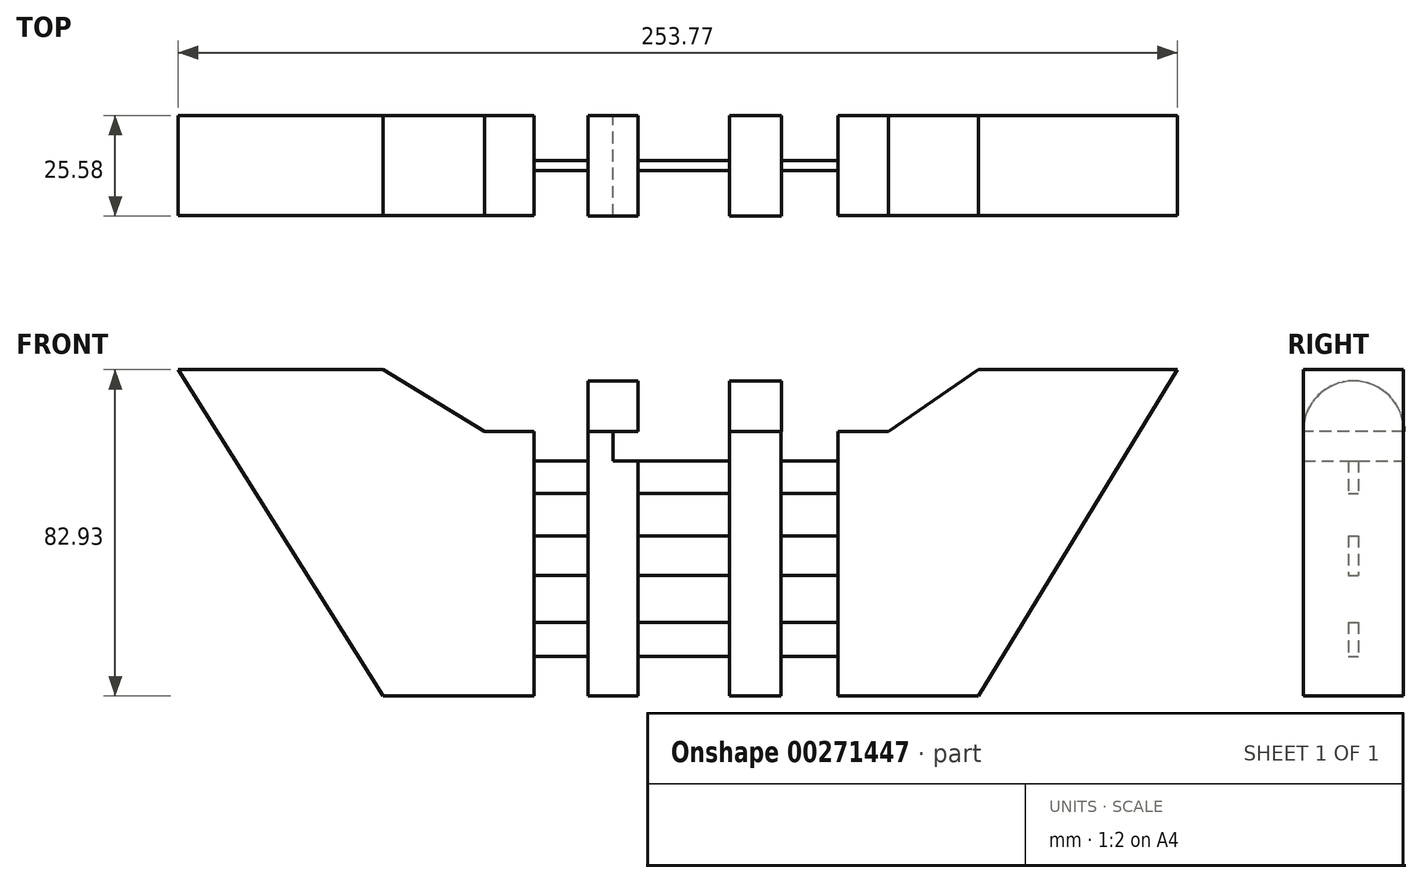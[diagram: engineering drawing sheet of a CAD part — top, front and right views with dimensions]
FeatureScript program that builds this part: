
annotation { "Feature Type Name" : "Feature", "Feature Type Description" : "" }
export const myFeature = defineFeature(function(context is Context, id is Id, definition is map)
    precondition{}
    {
        {
            var Q0;
            Q0=qCreatedBy(makeId("Front.planeOp"),FACE);
            var sketch = newSketch(context, id + "F0", { "sketchPlane" : qUnion([Q0])});
            skLineSegment(sketch, "E0", {"start": v(-135.53, 39.83) * mm, "end": v(-135.53, -55.88) * mm});
            skLineSegment(sketch, "E1", {"start": v(-135.53, -55.88) * mm, "end": v(134.04, -55.88) * mm});
            skLineSegment(sketch, "E2", {"start": v(134.04, -55.88) * mm, "end": v(134.04, 39.83) * mm});
            skLineSegment(sketch, "E3", {"start": v(-135.53, 39.83) * mm, "end": v(-75.5, -55.88) * mm});
            skLineSegment(sketch, "E4", {"start": v(134.04, 39.83) * mm, "end": v(75.79, -55.88) * mm});
            skLineSegment(sketch, "E5", {"start": v(-135.53, 27.05) * mm, "end": v(134.04, 27.05) * mm});
            skLineSegment(sketch, "E6", {"start": v(-75.5, 27.05) * mm, "end": v(-49.76, 11.38) * mm});
            skLineSegment(sketch, "E7", {"start": v(-49.76, 11.38) * mm, "end": v(-37.15, 11.38) * mm});
            skLineSegment(sketch, "E8", {"start": v(-37.15, 11.38) * mm, "end": v(-37.15, -55.88) * mm});
            skLineSegment(sketch, "E9", {"start": v(75.79, 27.05) * mm, "end": v(52.9, 11.38) * mm});
            skPoint(sketch, "E9.endSnap0", {"position": v(-43.46, 11.38) * mm});
            skLineSegment(sketch, "E10", {"start": v(52.9, 11.38) * mm, "end": v(40.12, 11.38) * mm});
            skLineSegment(sketch, "E11", {"start": v(40.12, 11.38) * mm, "end": v(40.12, -55.88) * mm});
            skLineSegment(sketch, "E12", {"start": v(-37.15, 11.38) * mm, "end": v(40.12, 11.38) * mm});
            skLineSegment(sketch, "E13", {"start": v(-23.48, -55.88) * mm, "end": v(-23.48, 11.38) * mm});
            skLineSegment(sketch, "E14", {"start": v(-23.48, 11.38) * mm, "end": v(-10.7, 11.38) * mm});
            skLineSegment(sketch, "E15", {"start": v(-10.7, 11.38) * mm, "end": v(-10.7, -55.88) * mm});
            skLineSegment(sketch, "E16", {"start": v(25.56, -55.88) * mm, "end": v(25.56, 11.38) * mm});
            skLineSegment(sketch, "E17", {"start": v(25.56, 11.38) * mm, "end": v(12.48, 11.38) * mm});
            skLineSegment(sketch, "E18", {"start": v(12.48, 11.38) * mm, "end": v(12.48, -55.88) * mm});
            skLineSegment(sketch, "E19", {"start": v(-23.48, 11.38) * mm, "end": v(-23.48, 16.64) * mm});
            skLineSegment(sketch, "E20", {"start": v(-23.48, 16.64) * mm, "end": v(-10.7, 16.64) * mm});
            skLineSegment(sketch, "E21", {"start": v(-10.7, 16.64) * mm, "end": v(-10.7, 11.38) * mm});
            skLineSegment(sketch, "E22", {"start": v(12.48, 11.38) * mm, "end": v(12.48, 16.64) * mm});
            skLineSegment(sketch, "E23", {"start": v(12.48, 16.64) * mm, "end": v(25.56, 16.64) * mm});
            skLineSegment(sketch, "E24", {"start": v(25.56, 16.64) * mm, "end": v(25.56, 11.38) * mm});
            skLineSegment(sketch, "E25", {"start": v(-37.15, 3.86) * mm, "end": v(40.12, 3.86) * mm});
            skLineSegment(sketch, "E26", {"start": v(-37.15, -4.46) * mm, "end": v(40.12, -4.46) * mm});
            skLineSegment(sketch, "E27", {"start": v(-37.15, -15.16) * mm, "end": v(40.12, -15.16) * mm});
            skLineSegment(sketch, "E28", {"start": v(-37.15, -25.26) * mm, "end": v(40.12, -25.26) * mm});
            skLineSegment(sketch, "E29", {"start": v(-37.15, -37.15) * mm, "end": v(40.12, -37.15) * mm});
            skLineSegment(sketch, "E30", {"start": v(-37.15, -45.77) * mm, "end": v(40.12, -45.77) * mm});
            skLineSegment(sketch, "E31", {"start": v(-17.09, -55.88) * mm, "end": v(-17.09, 35.3) * mm});
            skPoint(sketch, "E31.startSnap0", {"position": v(-17.09, 11.38) * mm});
            skLineSegment(sketch, "E32", {"start": v(19.02, -55.88) * mm, "end": v(19.02, 35.3) * mm});
            skPoint(sketch, "E32.startSnap0", {"position": v(19.02, 11.38) * mm});
            skLineSegment(sketch, "E33.bottom", {"start": v(-23.48, 11.38) * mm, "end": v(-10.72, 11.38) * mm});
            skLineSegment(sketch, "E33.top", {"start": v(-23.48, 24.18) * mm, "end": v(-10.72, 24.18) * mm});
            skLineSegment(sketch, "E33.left", {"start": v(-23.48, 11.38) * mm, "end": v(-23.48, 24.18) * mm});
            skLineSegment(sketch, "E33.right", {"start": v(-10.72, 11.38) * mm, "end": v(-10.72, 24.18) * mm});
            skLineSegment(sketch, "E34.bottom", {"start": v(12.48, 11.38) * mm, "end": v(25.74, 11.38) * mm});
            skLineSegment(sketch, "E34.top", {"start": v(12.48, 24.18) * mm, "end": v(25.74, 24.18) * mm});
            skLineSegment(sketch, "E34.left", {"start": v(12.48, 11.38) * mm, "end": v(12.48, 24.18) * mm});
            skLineSegment(sketch, "E34.right", {"start": v(25.74, 11.38) * mm, "end": v(25.74, 24.18) * mm});
            skSolve(sketch);
        }
        {
            var Q0;
            {var subQ4=sQuery(id+"F0.wireOp",EDGE,"E6");Q0=makeQuery(id+"F0.imprint","IMPRINT",FACE,{"disambiguationData":[TD([[makeQuery(id+"F0.imprint","IMPRINT",EDGE,{"derivedFrom":subQ4}),-1.0]])]});}
            var Q1;
            {var subQ5=sQuery(id+"F0.wireOp",EDGE,"E9");Q1=makeQuery(id+"F0.imprint","IMPRINT",FACE,{"disambiguationData":[TD([[makeQuery(id+"F0.imprint","IMPRINT",EDGE,{"derivedFrom":subQ5}),1.0]])]});}
            var Q2;
            {var subQ0=sQuery(id+"F0.wireOp",EDGE,"E27");var subQ1=sQuery(id+"F0.wireOp",EDGE,"E13");var subQ2=makeQuery(id+"F0.imprint","INTERSECT",VERTEX,{"derivedFrom":[subQ1,subQ0]});Q2=makeQuery(id+"F0.imprint","IMPRINT",FACE,{"disambiguationData":[TD([[makeQuery(id+"F0.imprint","IMPRINT",EDGE,{"disambiguationData":[TD([[subQ2,-1.0]])],"derivedFrom":subQ1}),-1.0]])]});}
            var Q3;
            {var subQ0=sQuery(id+"F0.wireOp",EDGE,"E26");var subQ1=sQuery(id+"F0.wireOp",EDGE,"E13");var subQ2=makeQuery(id+"F0.imprint","INTERSECT",VERTEX,{"derivedFrom":[subQ1,subQ0]});Q3=makeQuery(id+"F0.imprint","IMPRINT",FACE,{"disambiguationData":[TD([[makeQuery(id+"F0.imprint","IMPRINT",EDGE,{"disambiguationData":[TD([[subQ2,-1.0]])],"derivedFrom":subQ1}),-1.0]])]});}
            var Q4;
            {var subQ0=sQuery(id+"F0.wireOp",EDGE,"E28");var subQ1=sQuery(id+"F0.wireOp",EDGE,"E13");var subQ2=makeQuery(id+"F0.imprint","INTERSECT",VERTEX,{"derivedFrom":[subQ1,subQ0]});Q4=makeQuery(id+"F0.imprint","IMPRINT",FACE,{"disambiguationData":[TD([[makeQuery(id+"F0.imprint","IMPRINT",EDGE,{"disambiguationData":[TD([[subQ2,-1.0]])],"derivedFrom":subQ1}),-1.0]])]});}
            var Q5;
            {var subQ0=sQuery(id+"F0.wireOp",EDGE,"E29");var subQ1=sQuery(id+"F0.wireOp",EDGE,"E13");var subQ2=makeQuery(id+"F0.imprint","INTERSECT",VERTEX,{"derivedFrom":[subQ1,subQ0]});Q5=makeQuery(id+"F0.imprint","IMPRINT",FACE,{"disambiguationData":[TD([[makeQuery(id+"F0.imprint","IMPRINT",EDGE,{"disambiguationData":[TD([[subQ2,-1.0]])],"derivedFrom":subQ1}),-1.0]])]});}
            var Q6;
            {var subQ0=sQuery(id+"F0.wireOp",EDGE,"E30");var subQ1=sQuery(id+"F0.wireOp",EDGE,"E13");var subQ2=makeQuery(id+"F0.imprint","INTERSECT",VERTEX,{"derivedFrom":[subQ1,subQ0]});Q6=makeQuery(id+"F0.imprint","IMPRINT",FACE,{"disambiguationData":[TD([[makeQuery(id+"F0.imprint","IMPRINT",EDGE,{"disambiguationData":[TD([[subQ2,-1.0]])],"derivedFrom":subQ1}),-1.0]])]});}
            var Q7;
            {var subQ0=sQuery(id+"F0.wireOp",EDGE,"E13");var subQ1=sQuery(id+"F0.wireOp",EDGE,"E1");var subQ2=makeQuery(id+"F0.imprint","INTERSECT",VERTEX,{"derivedFrom":[subQ1,subQ0]});Q7=makeQuery(id+"F0.imprint","IMPRINT",FACE,{"disambiguationData":[TD([[makeQuery(id+"F0.imprint","IMPRINT",EDGE,{"disambiguationData":[TD([[subQ2,-1.0]])],"derivedFrom":subQ1}),1.0]])]});}
            var Q8;
            {var subQ0=sQuery(id+"F0.wireOp",EDGE,"E17");Q8=makeQuery(id+"F0.imprint","IMPRINT",FACE,{"disambiguationData":[TD([[makeQuery(id+"F0.imprint","IMPRINT",EDGE,{"derivedFrom":subQ0}),1.0]])]});}
            var Q9;
            {var subQ0=sQuery(id+"F0.wireOp",EDGE,"E26");var subQ1=sQuery(id+"F0.wireOp",EDGE,"E16");var subQ2=makeQuery(id+"F0.imprint","INTERSECT",VERTEX,{"derivedFrom":[subQ1,subQ0]});Q9=makeQuery(id+"F0.imprint","IMPRINT",FACE,{"disambiguationData":[TD([[makeQuery(id+"F0.imprint","IMPRINT",EDGE,{"disambiguationData":[TD([[subQ2,-1.0]])],"derivedFrom":subQ1}),1.0]])]});}
            var Q10;
            {var subQ0=sQuery(id+"F0.wireOp",EDGE,"E27");var subQ1=sQuery(id+"F0.wireOp",EDGE,"E16");var subQ2=makeQuery(id+"F0.imprint","INTERSECT",VERTEX,{"derivedFrom":[subQ1,subQ0]});Q10=makeQuery(id+"F0.imprint","IMPRINT",FACE,{"disambiguationData":[TD([[makeQuery(id+"F0.imprint","IMPRINT",EDGE,{"disambiguationData":[TD([[subQ2,-1.0]])],"derivedFrom":subQ1}),1.0]])]});}
            var Q11;
            {var subQ0=sQuery(id+"F0.wireOp",EDGE,"E28");var subQ1=sQuery(id+"F0.wireOp",EDGE,"E16");var subQ2=makeQuery(id+"F0.imprint","INTERSECT",VERTEX,{"derivedFrom":[subQ1,subQ0]});Q11=makeQuery(id+"F0.imprint","IMPRINT",FACE,{"disambiguationData":[TD([[makeQuery(id+"F0.imprint","IMPRINT",EDGE,{"disambiguationData":[TD([[subQ2,-1.0]])],"derivedFrom":subQ1}),1.0]])]});}
            var Q12;
            {var subQ0=sQuery(id+"F0.wireOp",EDGE,"E29");var subQ1=sQuery(id+"F0.wireOp",EDGE,"E16");var subQ2=makeQuery(id+"F0.imprint","INTERSECT",VERTEX,{"derivedFrom":[subQ1,subQ0]});Q12=makeQuery(id+"F0.imprint","IMPRINT",FACE,{"disambiguationData":[TD([[makeQuery(id+"F0.imprint","IMPRINT",EDGE,{"disambiguationData":[TD([[subQ2,-1.0]])],"derivedFrom":subQ1}),1.0]])]});}
            var Q13;
            {var subQ0=sQuery(id+"F0.wireOp",EDGE,"E30");var subQ1=sQuery(id+"F0.wireOp",EDGE,"E16");var subQ2=makeQuery(id+"F0.imprint","INTERSECT",VERTEX,{"derivedFrom":[subQ1,subQ0]});Q13=makeQuery(id+"F0.imprint","IMPRINT",FACE,{"disambiguationData":[TD([[makeQuery(id+"F0.imprint","IMPRINT",EDGE,{"disambiguationData":[TD([[subQ2,-1.0]])],"derivedFrom":subQ1}),1.0]])]});}
            var Q14;
            {var subQ0=sQuery(id+"F0.wireOp",EDGE,"E16");var subQ1=sQuery(id+"F0.wireOp",EDGE,"E1");var subQ2=makeQuery(id+"F0.imprint","INTERSECT",VERTEX,{"derivedFrom":[subQ1,subQ0]});Q14=makeQuery(id+"F0.imprint","IMPRINT",FACE,{"disambiguationData":[TD([[makeQuery(id+"F0.imprint","IMPRINT",EDGE,{"disambiguationData":[TD([[subQ2,1.0]])],"derivedFrom":subQ1}),1.0]])]});}
            var Q15;
            {var subQ0=sQuery(id+"F0.wireOp",EDGE,"E14");Q15=makeQuery(id+"F0.imprint","IMPRINT",FACE,{"disambiguationData":[TD([[makeQuery(id+"F0.imprint","IMPRINT",EDGE,{"derivedFrom":subQ0}),-1.0]])]});}
            var Q16;
            {var subQ0=sQuery(id+"F0.wireOp",EDGE,"E25");var subQ1=sQuery(id+"F0.wireOp",EDGE,"E15");var subQ2=makeQuery(id+"F0.imprint","INTERSECT",VERTEX,{"derivedFrom":[subQ1,subQ0]});Q16=makeQuery(id+"F0.imprint","IMPRINT",FACE,{"disambiguationData":[TD([[makeQuery(id+"F0.imprint","IMPRINT",EDGE,{"disambiguationData":[TD([[subQ2,-1.0]])],"derivedFrom":subQ1}),-1.0]])]});}
            var Q17;
            {var subQ0=sQuery(id+"F0.wireOp",EDGE,"E26");var subQ1=sQuery(id+"F0.wireOp",EDGE,"E15");var subQ2=makeQuery(id+"F0.imprint","INTERSECT",VERTEX,{"derivedFrom":[subQ1,subQ0]});Q17=makeQuery(id+"F0.imprint","IMPRINT",FACE,{"disambiguationData":[TD([[makeQuery(id+"F0.imprint","IMPRINT",EDGE,{"disambiguationData":[TD([[subQ2,-1.0]])],"derivedFrom":subQ1}),-1.0]])]});}
            var Q18;
            {var subQ0=sQuery(id+"F0.wireOp",EDGE,"E27");var subQ1=sQuery(id+"F0.wireOp",EDGE,"E15");var subQ2=makeQuery(id+"F0.imprint","INTERSECT",VERTEX,{"derivedFrom":[subQ1,subQ0]});Q18=makeQuery(id+"F0.imprint","IMPRINT",FACE,{"disambiguationData":[TD([[makeQuery(id+"F0.imprint","IMPRINT",EDGE,{"disambiguationData":[TD([[subQ2,-1.0]])],"derivedFrom":subQ1}),-1.0]])]});}
            var Q19;
            {var subQ0=sQuery(id+"F0.wireOp",EDGE,"E28");var subQ1=sQuery(id+"F0.wireOp",EDGE,"E15");var subQ2=makeQuery(id+"F0.imprint","INTERSECT",VERTEX,{"derivedFrom":[subQ1,subQ0]});Q19=makeQuery(id+"F0.imprint","IMPRINT",FACE,{"disambiguationData":[TD([[makeQuery(id+"F0.imprint","IMPRINT",EDGE,{"disambiguationData":[TD([[subQ2,-1.0]])],"derivedFrom":subQ1}),-1.0]])]});}
            var Q20;
            {var subQ0=sQuery(id+"F0.wireOp",EDGE,"E29");var subQ1=sQuery(id+"F0.wireOp",EDGE,"E15");var subQ2=makeQuery(id+"F0.imprint","INTERSECT",VERTEX,{"derivedFrom":[subQ1,subQ0]});Q20=makeQuery(id+"F0.imprint","IMPRINT",FACE,{"disambiguationData":[TD([[makeQuery(id+"F0.imprint","IMPRINT",EDGE,{"disambiguationData":[TD([[subQ2,-1.0]])],"derivedFrom":subQ1}),-1.0]])]});}
            var Q21;
            {var subQ0=sQuery(id+"F0.wireOp",EDGE,"E15");var subQ1=sQuery(id+"F0.wireOp",EDGE,"E1");var subQ2=makeQuery(id+"F0.imprint","INTERSECT",VERTEX,{"derivedFrom":[subQ1,subQ0]});Q21=makeQuery(id+"F0.imprint","IMPRINT",FACE,{"disambiguationData":[TD([[makeQuery(id+"F0.imprint","IMPRINT",EDGE,{"disambiguationData":[TD([[subQ2,1.0]])],"derivedFrom":subQ1}),1.0]])]});}
            var Q22;
            {var subQ0=sQuery(id+"F0.wireOp",EDGE,"E25");var subQ1=sQuery(id+"F0.wireOp",EDGE,"E18");var subQ2=makeQuery(id+"F0.imprint","INTERSECT",VERTEX,{"derivedFrom":[subQ1,subQ0]});Q22=makeQuery(id+"F0.imprint","IMPRINT",FACE,{"disambiguationData":[TD([[makeQuery(id+"F0.imprint","IMPRINT",EDGE,{"disambiguationData":[TD([[subQ2,-1.0]])],"derivedFrom":subQ1}),1.0]])]});}
            var Q23;
            {var subQ0=sQuery(id+"F0.wireOp",EDGE,"E26");var subQ1=sQuery(id+"F0.wireOp",EDGE,"E18");var subQ2=makeQuery(id+"F0.imprint","INTERSECT",VERTEX,{"derivedFrom":[subQ1,subQ0]});Q23=makeQuery(id+"F0.imprint","IMPRINT",FACE,{"disambiguationData":[TD([[makeQuery(id+"F0.imprint","IMPRINT",EDGE,{"disambiguationData":[TD([[subQ2,-1.0]])],"derivedFrom":subQ1}),1.0]])]});}
            var Q24;
            {var subQ0=sQuery(id+"F0.wireOp",EDGE,"E27");var subQ1=sQuery(id+"F0.wireOp",EDGE,"E18");var subQ2=makeQuery(id+"F0.imprint","INTERSECT",VERTEX,{"derivedFrom":[subQ1,subQ0]});Q24=makeQuery(id+"F0.imprint","IMPRINT",FACE,{"disambiguationData":[TD([[makeQuery(id+"F0.imprint","IMPRINT",EDGE,{"disambiguationData":[TD([[subQ2,-1.0]])],"derivedFrom":subQ1}),1.0]])]});}
            var Q25;
            {var subQ0=sQuery(id+"F0.wireOp",EDGE,"E28");var subQ1=sQuery(id+"F0.wireOp",EDGE,"E18");var subQ2=makeQuery(id+"F0.imprint","INTERSECT",VERTEX,{"derivedFrom":[subQ1,subQ0]});Q25=makeQuery(id+"F0.imprint","IMPRINT",FACE,{"disambiguationData":[TD([[makeQuery(id+"F0.imprint","IMPRINT",EDGE,{"disambiguationData":[TD([[subQ2,-1.0]])],"derivedFrom":subQ1}),1.0]])]});}
            var Q26;
            {var subQ0=sQuery(id+"F0.wireOp",EDGE,"E29");var subQ1=sQuery(id+"F0.wireOp",EDGE,"E18");var subQ2=makeQuery(id+"F0.imprint","INTERSECT",VERTEX,{"derivedFrom":[subQ1,subQ0]});Q26=makeQuery(id+"F0.imprint","IMPRINT",FACE,{"disambiguationData":[TD([[makeQuery(id+"F0.imprint","IMPRINT",EDGE,{"disambiguationData":[TD([[subQ2,-1.0]])],"derivedFrom":subQ1}),1.0]])]});}
            var Q27;
            {var subQ0=sQuery(id+"F0.wireOp",EDGE,"E18");var subQ1=sQuery(id+"F0.wireOp",EDGE,"E1");var subQ2=makeQuery(id+"F0.imprint","INTERSECT",VERTEX,{"derivedFrom":[subQ1,subQ0]});Q27=makeQuery(id+"F0.imprint","IMPRINT",FACE,{"disambiguationData":[TD([[makeQuery(id+"F0.imprint","IMPRINT",EDGE,{"disambiguationData":[TD([[subQ2,-1.0]])],"derivedFrom":subQ1}),1.0]])]});}
            var Q28;
            {var subQ1=sQuery(id+"F0.wireOp",EDGE,"E13");var subQ3=sQuery(id+"F0.wireOp",EDGE,"E25");var subQ4=makeQuery(id+"F0.imprint","INTERSECT",VERTEX,{"derivedFrom":[subQ1,subQ3]});Q28=makeQuery(id+"F0.imprint","IMPRINT",FACE,{"disambiguationData":[TD([[makeQuery(id+"F0.imprint","IMPRINT",EDGE,{"disambiguationData":[TD([[subQ4,-1.0]])],"derivedFrom":subQ3}),1.0]])]});}
            var Q29;
            {var subQ1=sQuery(id+"F0.wireOp",EDGE,"E18");var subQ3=sQuery(id+"F0.wireOp",EDGE,"E25");var subQ4=makeQuery(id+"F0.imprint","INTERSECT",VERTEX,{"derivedFrom":[subQ1,subQ3]});Q29=makeQuery(id+"F0.imprint","IMPRINT",FACE,{"disambiguationData":[TD([[makeQuery(id+"F0.imprint","IMPRINT",EDGE,{"disambiguationData":[TD([[subQ4,-1.0]])],"derivedFrom":subQ3}),1.0]])]});}
            var Q30;
            {var subQ1=sQuery(id+"F0.wireOp",EDGE,"E16");var subQ3=sQuery(id+"F0.wireOp",EDGE,"E25");var subQ4=makeQuery(id+"F0.imprint","INTERSECT",VERTEX,{"derivedFrom":[subQ1,subQ3]});Q30=makeQuery(id+"F0.imprint","IMPRINT",FACE,{"disambiguationData":[TD([[makeQuery(id+"F0.imprint","IMPRINT",EDGE,{"disambiguationData":[TD([[subQ4,1.0]])],"derivedFrom":subQ3}),1.0]])]});}
            extrude(context, id + "F1", {"entities" : qUnion([Q0, Q1, Q2, Q3, Q4, Q5, Q6, Q7, Q8, Q9, Q10, Q11, Q12, Q13, Q14, Q15, Q16, Q17, Q18, Q19, Q20, Q21, Q22, Q23, Q24, Q25, Q26, Q27, Q28, Q29, Q30]), "endBound" : BoundingType.SYMMETRIC, "depth" : 25.4 * mm});
        }
        {
            var Q0;
            {var subQ0=sQuery(id+"F0.wireOp",EDGE,"E25");var subQ1=sQuery(id+"F0.wireOp",EDGE,"E8");var subQ2=makeQuery(id+"F0.imprint","INTERSECT",VERTEX,{"derivedFrom":[subQ1,subQ0]});Q0=makeQuery(id+"F0.imprint","IMPRINT",FACE,{"disambiguationData":[TD([[makeQuery(id+"F0.imprint","IMPRINT",EDGE,{"disambiguationData":[TD([[subQ2,-1.0]])],"derivedFrom":subQ1}),1.0]])]});}
            var Q1;
            {var subQ0=sQuery(id+"F0.wireOp",EDGE,"E25");var subQ1=sQuery(id+"F0.wireOp",EDGE,"E15");var subQ2=makeQuery(id+"F0.imprint","INTERSECT",VERTEX,{"derivedFrom":[subQ1,subQ0]});Q1=makeQuery(id+"F0.imprint","IMPRINT",FACE,{"disambiguationData":[TD([[makeQuery(id+"F0.imprint","IMPRINT",EDGE,{"disambiguationData":[TD([[subQ2,-1.0]])],"derivedFrom":subQ1}),1.0]])]});}
            var Q2;
            {var subQ0=sQuery(id+"F0.wireOp",EDGE,"E25");var subQ1=sQuery(id+"F0.wireOp",EDGE,"E11");var subQ2=makeQuery(id+"F0.imprint","INTERSECT",VERTEX,{"derivedFrom":[subQ1,subQ0]});Q2=makeQuery(id+"F0.imprint","IMPRINT",FACE,{"disambiguationData":[TD([[makeQuery(id+"F0.imprint","IMPRINT",EDGE,{"disambiguationData":[TD([[subQ2,-1.0]])],"derivedFrom":subQ1}),-1.0]])]});}
            var Q3;
            {var subQ0=sQuery(id+"F0.wireOp",EDGE,"E27");var subQ1=sQuery(id+"F0.wireOp",EDGE,"E8");var subQ2=makeQuery(id+"F0.imprint","INTERSECT",VERTEX,{"derivedFrom":[subQ1,subQ0]});Q3=makeQuery(id+"F0.imprint","IMPRINT",FACE,{"disambiguationData":[TD([[makeQuery(id+"F0.imprint","IMPRINT",EDGE,{"disambiguationData":[TD([[subQ2,-1.0]])],"derivedFrom":subQ1}),1.0]])]});}
            var Q4;
            {var subQ0=sQuery(id+"F0.wireOp",EDGE,"E29");var subQ1=sQuery(id+"F0.wireOp",EDGE,"E8");var subQ2=makeQuery(id+"F0.imprint","INTERSECT",VERTEX,{"derivedFrom":[subQ1,subQ0]});Q4=makeQuery(id+"F0.imprint","IMPRINT",FACE,{"disambiguationData":[TD([[makeQuery(id+"F0.imprint","IMPRINT",EDGE,{"disambiguationData":[TD([[subQ2,-1.0]])],"derivedFrom":subQ1}),1.0]])]});}
            var Q5;
            {var subQ0=sQuery(id+"F0.wireOp",EDGE,"E27");var subQ1=sQuery(id+"F0.wireOp",EDGE,"E15");var subQ2=makeQuery(id+"F0.imprint","INTERSECT",VERTEX,{"derivedFrom":[subQ1,subQ0]});Q5=makeQuery(id+"F0.imprint","IMPRINT",FACE,{"disambiguationData":[TD([[makeQuery(id+"F0.imprint","IMPRINT",EDGE,{"disambiguationData":[TD([[subQ2,-1.0]])],"derivedFrom":subQ1}),1.0]])]});}
            var Q6;
            {var subQ0=sQuery(id+"F0.wireOp",EDGE,"E29");var subQ1=sQuery(id+"F0.wireOp",EDGE,"E15");var subQ2=makeQuery(id+"F0.imprint","INTERSECT",VERTEX,{"derivedFrom":[subQ1,subQ0]});Q6=makeQuery(id+"F0.imprint","IMPRINT",FACE,{"disambiguationData":[TD([[makeQuery(id+"F0.imprint","IMPRINT",EDGE,{"disambiguationData":[TD([[subQ2,-1.0]])],"derivedFrom":subQ1}),1.0]])]});}
            var Q7;
            {var subQ0=sQuery(id+"F0.wireOp",EDGE,"E27");var subQ1=sQuery(id+"F0.wireOp",EDGE,"E11");var subQ2=makeQuery(id+"F0.imprint","INTERSECT",VERTEX,{"derivedFrom":[subQ1,subQ0]});Q7=makeQuery(id+"F0.imprint","IMPRINT",FACE,{"disambiguationData":[TD([[makeQuery(id+"F0.imprint","IMPRINT",EDGE,{"disambiguationData":[TD([[subQ2,-1.0]])],"derivedFrom":subQ1}),-1.0]])]});}
            var Q8;
            {var subQ0=sQuery(id+"F0.wireOp",EDGE,"E29");var subQ1=sQuery(id+"F0.wireOp",EDGE,"E11");var subQ2=makeQuery(id+"F0.imprint","INTERSECT",VERTEX,{"derivedFrom":[subQ1,subQ0]});Q8=makeQuery(id+"F0.imprint","IMPRINT",FACE,{"disambiguationData":[TD([[makeQuery(id+"F0.imprint","IMPRINT",EDGE,{"disambiguationData":[TD([[subQ2,-1.0]])],"derivedFrom":subQ1}),-1.0]])]});}
            extrude(context, id + "F2", {"entities" : qUnion([Q0, Q1, Q2, Q3, Q4, Q5, Q6, Q7, Q8]), "endBound" : BoundingType.SYMMETRIC, "depth" : 2.54 * mm});
        }
        {
            var Q0;
            {var subQ0=sQuery(id+"F0.wireOp",EDGE,"E33.left");var subQ1=sQuery(id+"F0.wireOp",EDGE,"E20");var subQ2=makeQuery(id+"F0.imprint","INTERSECT",VERTEX,{"derivedFrom":[subQ1,subQ0]});Q0=makeQuery(id+"F0.imprint","IMPRINT",FACE,{"disambiguationData":[TD([[makeQuery(id+"F0.imprint","IMPRINT",EDGE,{"disambiguationData":[TD([[subQ2,-1.0]])],"derivedFrom":subQ1}),1.0]])]});}
            var Q1;
            {var subQ0=sQuery(id+"F0.wireOp",EDGE,"E31");var subQ1=sQuery(id+"F0.wireOp",EDGE,"E20");var subQ2=makeQuery(id+"F0.imprint","INTERSECT",VERTEX,{"derivedFrom":[subQ1,subQ0]});Q1=makeQuery(id+"F0.imprint","IMPRINT",FACE,{"disambiguationData":[TD([[makeQuery(id+"F0.imprint","IMPRINT",EDGE,{"disambiguationData":[TD([[subQ2,-1.0]])],"derivedFrom":subQ1}),1.0]])]});}
            var Q2;
            {var subQ0=sQuery(id+"F0.wireOp",EDGE,"E33.left");var subQ1=sQuery(id+"F0.wireOp",EDGE,"E20");var subQ2=makeQuery(id+"F0.imprint","INTERSECT",VERTEX,{"derivedFrom":[subQ1,subQ0]});Q2=makeQuery(id+"F0.imprint","IMPRINT",FACE,{"disambiguationData":[TD([[makeQuery(id+"F0.imprint","IMPRINT",EDGE,{"disambiguationData":[TD([[subQ2,-1.0]])],"derivedFrom":subQ1}),-1.0]])]});}
            var Q3;
            {var subQ0=sQuery(id+"F0.wireOp",EDGE,"E31");var subQ1=sQuery(id+"F0.wireOp",EDGE,"E20");var subQ2=makeQuery(id+"F0.imprint","INTERSECT",VERTEX,{"derivedFrom":[subQ1,subQ0]});Q3=makeQuery(id+"F0.imprint","IMPRINT",FACE,{"disambiguationData":[TD([[makeQuery(id+"F0.imprint","IMPRINT",EDGE,{"disambiguationData":[TD([[subQ2,-1.0]])],"derivedFrom":subQ1}),-1.0]])]});}
            var Q4;
            Q4=sQuery(id+"F0.wireOp",EDGE,"E12");
            revolve(context, id + "F3", {"entities" : qUnion([Q0, Q1, Q2, Q3]), "axis" : qUnion([Q4]), "revolveType" : RevolveType.SYMMETRIC, "angle" : 180 * degree});
        }
        {
            var Q0;
            {var subQ0=sQuery(id+"F0.wireOp",EDGE,"E34.left");var subQ1=sQuery(id+"F0.wireOp",EDGE,"E23");var subQ2=makeQuery(id+"F0.imprint","INTERSECT",VERTEX,{"derivedFrom":[subQ1,subQ0]});Q0=makeQuery(id+"F0.imprint","IMPRINT",FACE,{"disambiguationData":[TD([[makeQuery(id+"F0.imprint","IMPRINT",EDGE,{"disambiguationData":[TD([[subQ2,-1.0]])],"derivedFrom":subQ1}),-1.0]])]});}
            var Q1;
            {var subQ0=sQuery(id+"F0.wireOp",EDGE,"E34.left");var subQ1=sQuery(id+"F0.wireOp",EDGE,"E23");var subQ2=makeQuery(id+"F0.imprint","INTERSECT",VERTEX,{"derivedFrom":[subQ1,subQ0]});Q1=makeQuery(id+"F0.imprint","IMPRINT",FACE,{"disambiguationData":[TD([[makeQuery(id+"F0.imprint","IMPRINT",EDGE,{"disambiguationData":[TD([[subQ2,-1.0]])],"derivedFrom":subQ1}),1.0]])]});}
            var Q2;
            {var subQ1=sQuery(id+"F0.wireOp",EDGE,"E24");Q2=makeQuery(id+"F0.imprint","IMPRINT",FACE,{"disambiguationData":[TD([[makeQuery(id+"F0.imprint","IMPRINT",EDGE,{"derivedFrom":subQ1}),1.0]])]});}
            var Q3;
            {var subQ0=sQuery(id+"F0.wireOp",EDGE,"E24");Q3=makeQuery(id+"F0.imprint","IMPRINT",FACE,{"disambiguationData":[TD([[makeQuery(id+"F0.imprint","IMPRINT",EDGE,{"derivedFrom":subQ0}),-1.0]])]});}
            var Q4;
            Q4=sQuery(id+"F0.wireOp",EDGE,"E12");
            revolve(context, id + "F4", {"entities" : qUnion([Q0, Q1, Q2, Q3]), "axis" : qUnion([Q4]), "revolveType" : RevolveType.SYMMETRIC, "angle" : 180 * degree});
        }
    });
